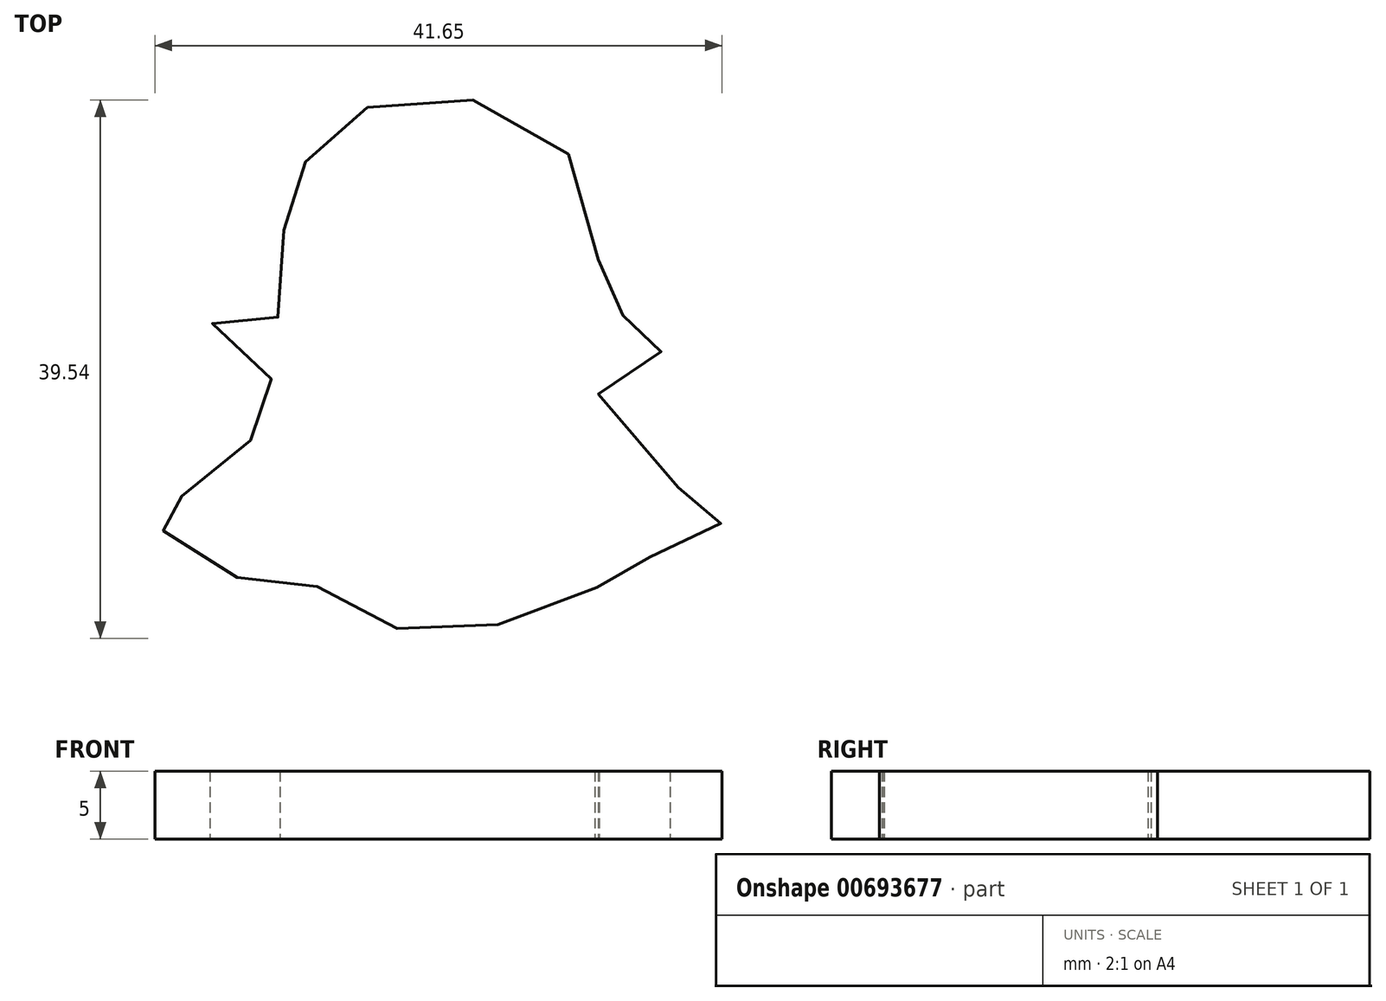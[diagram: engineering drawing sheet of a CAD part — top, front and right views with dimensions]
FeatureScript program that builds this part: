
annotation { "Feature Type Name" : "Feature", "Feature Type Description" : "" }
export const myFeature = defineFeature(function(context is Context, id is Id, definition is map)
    precondition{}
    {
        {
            var Q0;
            Q0=qCreatedBy(makeId("Top.planeOp"),FACE);
            var sketch = newSketch(context, id + "F0", { "sketchPlane" : qUnion([Q0])});
            skFitSpline(sketch, "E0", {"points": [v(-57.66, 46.3) * mm, v(-60.14, 44.6) * mm, v(-62.32, 42.19) * mm, v(-63.38, 40.24) * mm, v(-63.73, 38.6) * mm, v(-63.9, 32) * mm, v(-64.02, 31.3) * mm, v(-64.38, 30.82) * mm, v(-66.9, 31.3) * mm, v(-68.91, 30.65) * mm, v(-68.91, 28.94) * mm, v(-64.9, 26.52) * mm, v(-64.08, 25.17) * mm, v(-65.5, 22.87) * mm, v(-67.67, 20.1) * mm, v(-70.8, 17.93) * mm, v(-73.03, 17.34) * mm, v(-73.2, 16.7) * mm, v(-72.97, 15.45) * mm, v(-68.03, 13.69) * mm, v(-67.14, 11.69) * mm, v(-63.73, 11.1) * mm, v(-61.14, 11.1) * mm, v(-57.55, 9.1) * mm, v(-54.43, 7.74) * mm, v(-49.42, 7.68) * mm, v(-44.3, 10.68) * mm, v(-39.94, 10.98) * mm, v(-38.23, 11.1) * mm, v(-37.06, 13.16) * mm, v(-34, 14.51) * mm, v(-31.81, 15.57) * mm, v(-31.81, 17.1) * mm, v(-33, 17.7) * mm, v(-36.11, 19.22) * mm, v(-40.7, 25.23) * mm, v(-38.82, 27.17) * mm, v(-36.29, 28.23) * mm, v(-35.47, 29.94) * mm, v(-37.76, 31.3) * mm, v(-40.59, 30.65) * mm, v(-40.82, 33.88) * mm, v(-41.06, 39.65) * mm, v(-44.3, 44.37) * mm, v(-49.18, 46.78) * mm, v(-56.84, 46.43) * mm, v(-57.66, 46.3) * mm]});
            skSolve(sketch);
        }
        {
            var Q0;
            Q0 = qSketchRegion(id + "F0", true);
            extrude(context, id + "F1", {"entities" : qUnion([Q0]), "depth" : 5 * mm, "offsetDistance" : 25.4 * mm});
        }
    });
